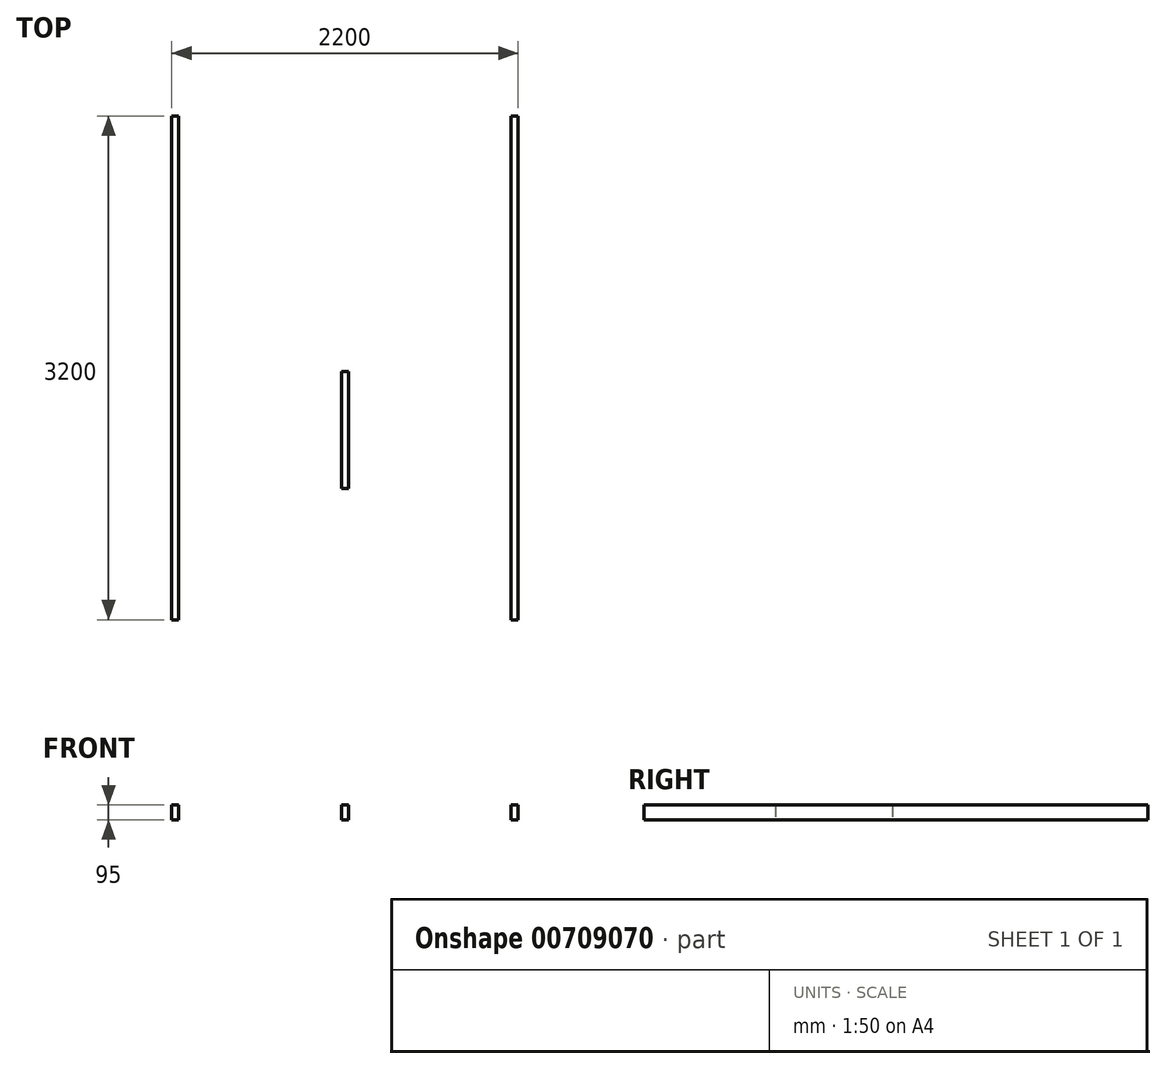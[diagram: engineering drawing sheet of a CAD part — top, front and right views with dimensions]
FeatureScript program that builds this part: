
annotation { "Feature Type Name" : "Feature", "Feature Type Description" : "" }
export const myFeature = defineFeature(function(context is Context, id is Id, definition is map)
    precondition{}
    {
        {
            var Q0;
            Q0=qCreatedBy(makeId("Top.planeOp"),FACE);
            var sketch = newSketch(context, id + "F0", { "sketchPlane" : qUnion([Q0])});
            skLineSegment(sketch, "E0.bottom", {"start": v(1100, 1600) * mm, "end": v(-1100, 1600) * mm});
            skLineSegment(sketch, "E0.top", {"start": v(1100, -1600) * mm, "end": v(-1100, -1600) * mm});
            skLineSegment(sketch, "E0.left", {"start": v(1100, 1600) * mm, "end": v(1100, -1600) * mm});
            skLineSegment(sketch, "E0.right", {"start": v(-1100, 1600) * mm, "end": v(-1100, -1600) * mm});
            skPoint(sketch, "E0.middle", {"position": v(0, 0) * mm});
            skLineSegment(sketch, "E1.bottom", {"start": v(-1055, -1600) * mm, "end": v(1055, -1600) * mm});
            skLineSegment(sketch, "E1.top", {"start": v(-1055, 1600) * mm, "end": v(1055, 1600) * mm});
            skLineSegment(sketch, "E1.left", {"start": v(-1055, -1600) * mm, "end": v(-1055, 1600) * mm});
            skLineSegment(sketch, "E1.right", {"start": v(1055, -1600) * mm, "end": v(1055, 1600) * mm});
            skLineSegment(sketch, "E2", {"start": v(-1055, 1555) * mm, "end": v(1055, 1555) * mm});
            skLineSegment(sketch, "E3", {"start": v(-1055, -1555) * mm, "end": v(1055, -1555) * mm});
            skLineSegment(sketch, "E4.left", {"start": v(-1055, 22.5) * mm, "end": v(-1055, -22.5) * mm});
            skLineSegment(sketch, "E4.right", {"start": v(1055, 22.5) * mm, "end": v(1055, -22.5) * mm});
            skLineSegment(sketch, "E5.top", {"start": v(-22.5, 1555) * mm, "end": v(22.5, 1555) * mm});
            skLineSegment(sketch, "E6.top", {"start": v(22.5, -1555) * mm, "end": v(-22.5, -1555) * mm});
            skLineSegment(sketch, "E7.bottom", {"start": v(-1055, 811.25) * mm, "end": v(1055, 811.25) * mm});
            skLineSegment(sketch, "E7.top", {"start": v(-1055, 766.25) * mm, "end": v(1055, 766.25) * mm});
            skLineSegment(sketch, "E7.left", {"start": v(-1055, 811.25) * mm, "end": v(-1055, 766.25) * mm});
            skLineSegment(sketch, "E7.right", {"start": v(1055, 811.25) * mm, "end": v(1055, 766.25) * mm});
            skLineSegment(sketch, "E8.bottom", {"start": v(-1055, -766.25) * mm, "end": v(1055, -766.25) * mm});
            skLineSegment(sketch, "E8.top", {"start": v(-1055, -811.25) * mm, "end": v(1055, -811.25) * mm});
            skLineSegment(sketch, "E8.left", {"start": v(-1055, -766.25) * mm, "end": v(-1055, -811.25) * mm});
            skLineSegment(sketch, "E8.right", {"start": v(1055, -766.25) * mm, "end": v(1055, -811.25) * mm});
            skLineSegment(sketch, "E9.bottom", {"start": v(1055, 22.5) * mm, "end": v(-1055, 22.5) * mm});
            skLineSegment(sketch, "E9.top", {"start": v(1055, -22.5) * mm, "end": v(-1055, -22.5) * mm});
            skLineSegment(sketch, "E10.bottom", {"start": v(22.5, 1555) * mm, "end": v(-22.5, 1555) * mm});
            skLineSegment(sketch, "E10.top", {"start": v(22.5, 811.25) * mm, "end": v(-22.5, 811.25) * mm});
            skLineSegment(sketch, "E10.left", {"start": v(22.5, 1555) * mm, "end": v(22.5, 811.25) * mm});
            skLineSegment(sketch, "E10.right", {"start": v(-22.5, 1555) * mm, "end": v(-22.5, 811.25) * mm});
            skLineSegment(sketch, "E11.bottom", {"start": v(22.5, 766.25) * mm, "end": v(-22.5, 766.25) * mm});
            skLineSegment(sketch, "E11.top", {"start": v(22.5, 22.5) * mm, "end": v(-22.5, 22.5) * mm});
            skLineSegment(sketch, "E11.left", {"start": v(22.5, 766.25) * mm, "end": v(22.5, 22.5) * mm});
            skLineSegment(sketch, "E11.right", {"start": v(-22.5, 766.25) * mm, "end": v(-22.5, 22.5) * mm});
            skLineSegment(sketch, "E12.MirrorCS", {"start": v(-22.5, -766.25) * mm, "end": v(-22.5, -22.5) * mm});
            skLineSegment(sketch, "E13.MirrorCS", {"start": v(22.5, -766.25) * mm, "end": v(22.5, -22.5) * mm});
            skLineSegment(sketch, "E14.MirrorCS", {"start": v(22.5, -1555) * mm, "end": v(22.5, -811.25) * mm});
            skLineSegment(sketch, "E15.MirrorCS", {"start": v(-22.5, -1555) * mm, "end": v(-22.5, -811.25) * mm});
            skSolve(sketch);
        }
        {
            var Q0;
            {var subQ5=sQuery(id+"F0.wireOp",EDGE,"E1.top");Q0=makeQuery(id+"F0.imprint","IMPRINT",FACE,{"disambiguationData":[TD([[makeQuery(id+"F0.imprint","IMPRINT",EDGE,{"derivedFrom":subQ5}),-1.0]])]});}
            var Q1;
            {var subQ8=sQuery(id+"F0.wireOp",EDGE,"E0.right");Q1=makeQuery(id+"F0.imprint","IMPRINT",FACE,{"disambiguationData":[TD([[makeQuery(id+"F0.imprint","IMPRINT",EDGE,{"derivedFrom":subQ8}),1.0]])]});}
            var Q2;
            {var subQ7=sQuery(id+"F0.wireOp",EDGE,"E0.left");Q2=makeQuery(id+"F0.imprint","IMPRINT",FACE,{"disambiguationData":[TD([[makeQuery(id+"F0.imprint","IMPRINT",EDGE,{"derivedFrom":subQ7}),-1.0]])]});}
            var Q3;
            {var subQ0=sQuery(id+"F0.wireOp",EDGE,"E12.MirrorCS");Q3=makeQuery(id+"F0.imprint","IMPRINT",FACE,{"disambiguationData":[TD([[makeQuery(id+"F0.imprint","IMPRINT",EDGE,{"derivedFrom":subQ0}),-1.0]])]});}
            var Q4;
            {var subQ0=sQuery(id+"F0.wireOp",EDGE,"E8.left");Q4=makeQuery(id+"F0.imprint","IMPRINT",FACE,{"disambiguationData":[TD([[makeQuery(id+"F0.imprint","IMPRINT",EDGE,{"derivedFrom":subQ0}),1.0]])]});}
            var Q5;
            Q5=makeQuery(id+"F0.imprint","IMPRINT",FACE,{"disambiguationData":[TD([[makeQuery(id+"F0.imprint","IMPRINT",EDGE,{"derivedFrom":sQuery(id+"F0.wireOp",EDGE,"E6.top")}),-1.0]])]});
            var Q6;
            {var subQ3=sQuery(id+"F0.wireOp",EDGE,"E4.right");Q6=makeQuery(id+"F0.imprint","IMPRINT",FACE,{"disambiguationData":[TD([[makeQuery(id+"F0.imprint","IMPRINT",EDGE,{"derivedFrom":subQ3}),-1.0]])]});}
            var Q7;
            {var subQ4=sQuery(id+"F0.wireOp",EDGE,"E7.left");Q7=makeQuery(id+"F0.imprint","IMPRINT",FACE,{"disambiguationData":[TD([[makeQuery(id+"F0.imprint","IMPRINT",EDGE,{"derivedFrom":subQ4}),1.0]])]});}
            var Q8;
            Q8=makeQuery(id+"F0.imprint","IMPRINT",FACE,{"disambiguationData":[TD([[makeQuery(id+"F0.imprint","IMPRINT",EDGE,{"derivedFrom":sQuery(id+"F0.wireOp",EDGE,"E11.bottom")}),1.0]])]});
            var Q9;
            Q9=makeQuery(id+"F0.imprint","IMPRINT",FACE,{"disambiguationData":[TD([[makeQuery(id+"F0.imprint","IMPRINT",EDGE,{"derivedFrom":sQuery(id+"F0.wireOp",EDGE,"E10.bottom")}),1.0]])]});
            var Q10;
            {var subQ5=sQuery(id+"F0.wireOp",EDGE,"E1.bottom");Q10=makeQuery(id+"F0.imprint","IMPRINT",FACE,{"disambiguationData":[TD([[makeQuery(id+"F0.imprint","IMPRINT",EDGE,{"derivedFrom":subQ5}),1.0]])]});}
            extrude(context, id + "F1", {"entities" : qUnion([Q0, Q1, Q2, Q3, Q4, Q5, Q6, Q7, Q8, Q9, Q10]), "depth" : 95 * mm, "offsetDistance" : 25 * mm});
        }
    });
